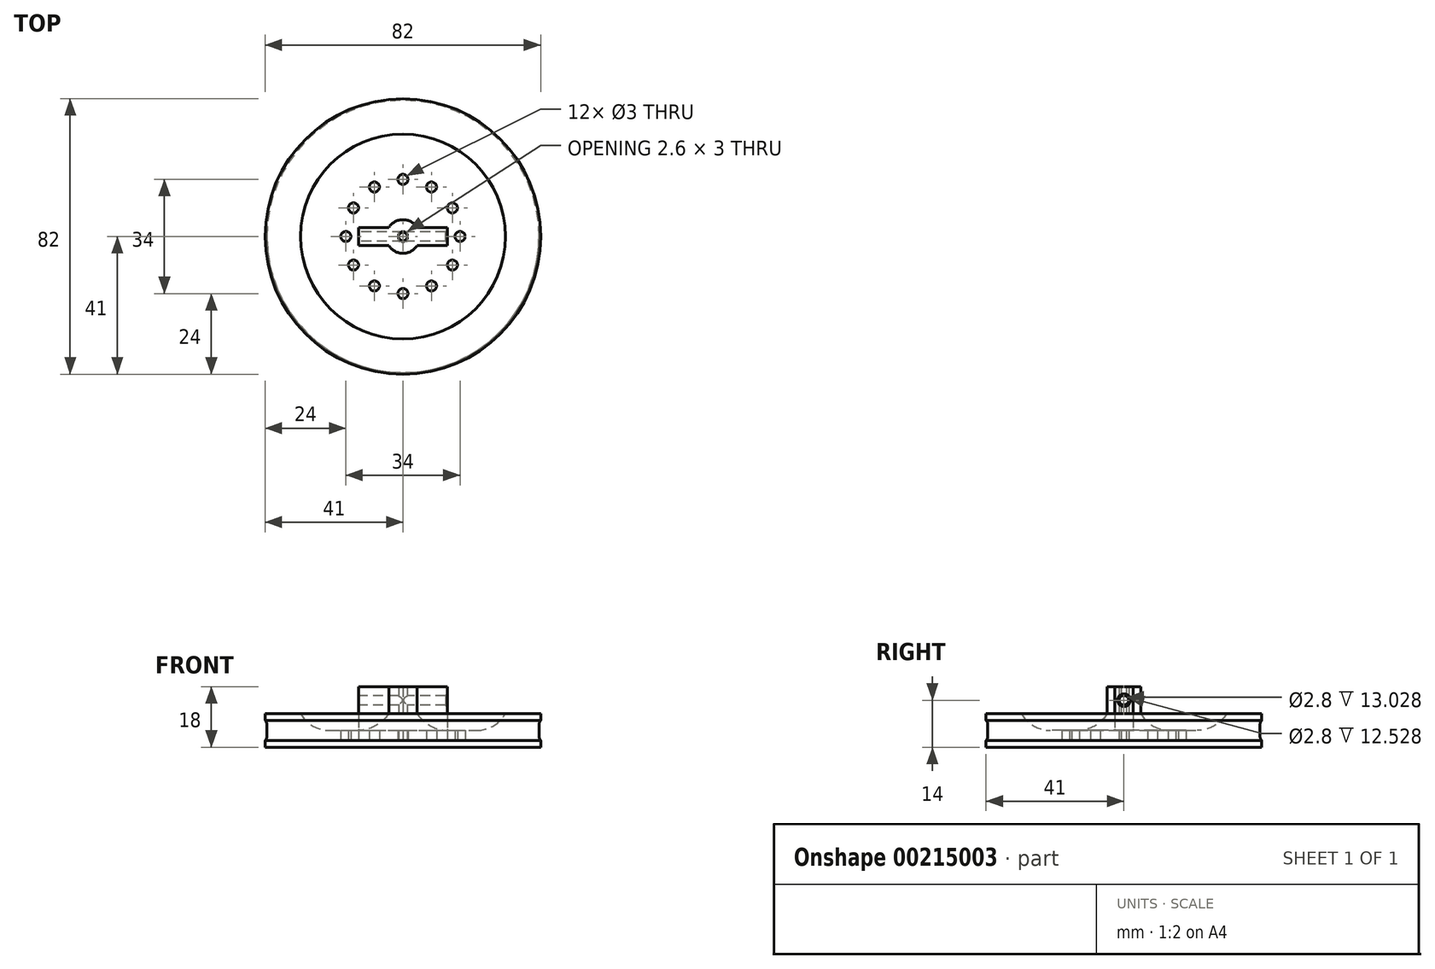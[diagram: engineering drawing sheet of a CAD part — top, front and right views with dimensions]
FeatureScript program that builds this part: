
annotation { "Feature Type Name" : "Feature", "Feature Type Description" : "" }
export const myFeature = defineFeature(function(context is Context, id is Id, definition is map)
    precondition{}
    {
        {
            var Q0;
            Q0=qCreatedBy(makeId("Front.planeOp"),FACE);
            var sketch = newSketch(context, id + "F0", { "sketchPlane" : qUnion([Q0])});
            skLineSegment(sketch, "E0", {"start": v(0, 0) * mm, "end": v(41, 0) * mm});
            skLineSegment(sketch, "E1", {"start": v(41, 10) * mm, "end": v(30.5, 10) * mm});
            skLineSegment(sketch, "E2", {"start": v(30.5, 10) * mm, "end": v(30.5, 5) * mm});
            skLineSegment(sketch, "E3", {"start": v(30.5, 5) * mm, "end": v(5, 5) * mm});
            skLineSegment(sketch, "E4", {"start": v(5, 5) * mm, "end": v(5, 10) * mm});
            skLineSegment(sketch, "E5", {"start": v(5, 10) * mm, "end": v(0, 10) * mm});
            skLineSegment(sketch, "E6", {"start": v(0, 10) * mm, "end": v(0, 0) * mm});
            skLineSegment(sketch, "E7", {"start": v(41, 0) * mm, "end": v(41, 2) * mm});
            skLineSegment(sketch, "E8", {"start": v(41, 2) * mm, "end": v(40.5, 2) * mm});
            skLineSegment(sketch, "E9", {"start": v(40.5, 2) * mm, "end": v(40.5, 8) * mm});
            skLineSegment(sketch, "E10", {"start": v(40.5, 8) * mm, "end": v(41, 8) * mm});
            skLineSegment(sketch, "E11", {"start": v(41, 8) * mm, "end": v(41, 10) * mm});
            skSolve(sketch);
        }
        {
            var Q0;
            Q0 = qSketchRegion(id + "F0", true);
            var Q1;
            Q1=sQuery(id+"F0.wireOp",EDGE,"E6");
            revolve(context, id + "F1", {"entities" : qUnion([Q0]), "axis" : qUnion([Q1]), "revolveType" : RevolveType.FULL});
        }
        {
            var Q0;
            Q0=makeQuery(id+"F1.opRevolve","SWEPT_EDGE",EDGE,{"disambiguationData":[OSD([sQuery(id+"F0.wireOp",EDGE,"E3"),sQuery(id+"F0.wireOp",EDGE,"E4")])]});
            fillet(context, id + "F2", {"entities" : qUnion([Q0]), "radius" : 10 * mm, "tangentPropagation" : true, "allowEdgeOverflow" : false});
        }
        {
            var Q0;
            Q0=makeQuery(id+"F1.opRevolve","SWEPT_EDGE",EDGE,{"disambiguationData":[OSD([sQuery(id+"F0.wireOp",EDGE,"E2"),sQuery(id+"F0.wireOp",EDGE,"E3")])]});
            fillet(context, id + "F3", {"entities" : qUnion([Q0]), "radius" : 10 * mm, "tangentPropagation" : true, "allowEdgeOverflow" : false});
        }
        {
            var Q0;
            Q0=makeQuery(id+"F1.opRevolve","SWEPT_FACE",FACE,{"disambiguationData":[OSD([sQuery(id+"F0.wireOp",EDGE,"E5")])]});
            var sketch = newSketch(context, id + "F4", { "sketchPlane" : qUnion([Q0])});
            skCircle(sketch, "E12.cCircle", {"center": v(0, 0) * mm, "radius": 1.5 * mm, "construction": true});
            skLineSegment(sketch, "E12.0", {"start": v(0, -1.5) * mm, "end": v(-1.3, -0.75) * mm});
            skLineSegment(sketch, "E12.1", {"start": v(-1.3, -0.75) * mm, "end": v(-1.3, 0.75) * mm});
            skLineSegment(sketch, "E12.2", {"start": v(-1.3, 0.75) * mm, "end": v(0, 1.5) * mm});
            skLineSegment(sketch, "E12.3", {"start": v(0, 1.5) * mm, "end": v(1.3, 0.75) * mm});
            skLineSegment(sketch, "E12.4", {"start": v(1.3, 0.75) * mm, "end": v(1.3, -0.75) * mm});
            skLineSegment(sketch, "E12.5", {"start": v(1.3, -0.75) * mm, "end": v(0, -1.5) * mm});
            skArc(sketch, "E13", {"start": v(-4.2, -2.71) * mm, "mid": v(5, 0) * mm, "end": v(-4.2, 2.71) * mm});
            skLineSegment(sketch, "E14", {"start": v(-4.2, -2.71) * mm, "end": v(-4.2, 2.71) * mm});
            skSolve(sketch);
        }
        {
            var Q0;
            Q0 = qSketchRegion(id + "F4", true);
            extrude(context, id + "F5", {"entities" : qUnion([Q0]), "operationType" : NewBodyOperationType.ADD, "depth" : 8 * mm});
        }
        {
            var Q0;
            Q0=makeQuery(id+"F5.opExtrude","SWEPT_FACE",FACE,{"disambiguationData":[OSD([sQuery(id+"F4.wireOp",EDGE,"E14")])]});
            extrude(context, id + "F6", {"entities" : qUnion([Q0]), "operationType" : NewBodyOperationType.ADD, "depth" : 9 * mm});
        }
        {
            var Q0;
            Q0=makeQuery(id+"F6.opExtrude","CAP_FACE",FACE,{"disambiguationData":[OSD([sQuery(id+"F4.wireOp",EDGE,"E14")])],"isStart":false});
            var sketch = newSketch(context, id + "F7", { "sketchPlane" : qUnion([Q0])});
            skCircle(sketch, "E15", {"center": v(0, 14) * mm, "radius": 1.4 * mm});
            skPoint(sketch, "E15.centerSnap0", {"position": v(0, 18) * mm});
            skSolve(sketch);
        }
        {
            var Q0;
            Q0 = qSketchRegion(id + "F7", true);
            extrude(context, id + "F8", {"entities" : qUnion([Q0]), "operationType" : NewBodyOperationType.REMOVE, "endBound" : BoundingType.THROUGH_ALL, "oppositeDirection" : true, "depth" : 25 * mm});
        }
        {
            var Q0;
            {var subQ0=sQuery(id+"F4.wireOp",EDGE,"E14");Q0=makeQuery(id+"F6.boolean.opBoolean","MERGE",FACE,{"derivedFrom":[makeQuery(id+"F5.opExtrude","CAP_FACE",FACE,{"disambiguationData":[OSD([sQuery(id+"F4.wireOp",EDGE,"E12.0"),sQuery(id+"F4.wireOp",EDGE,"E12.1"),sQuery(id+"F4.wireOp",EDGE,"E12.2"),sQuery(id+"F4.wireOp",EDGE,"E12.3"),sQuery(id+"F4.wireOp",EDGE,"E12.4"),sQuery(id+"F4.wireOp",EDGE,"E12.5"),sQuery(id+"F4.wireOp",EDGE,"E13"),subQ0])],"isStart":false}),makeQuery(id+"F6.opExtrude","SWEPT_FACE",FACE,{"disambiguationData":[OSD([subQ0]),TDD([makeQuery(id+"F5.opExtrude","CAP_EDGE",EDGE,{"disambiguationData":[OSD([subQ0])],"isStart":false})])]})]});}
            var sketch = newSketch(context, id + "F9", { "sketchPlane" : qUnion([Q0])});
            skLineSegment(sketch, "E16.0", {"start": v(1.3, -0.75) * mm, "end": v(0, -1.5) * mm});
            skLineSegment(sketch, "E16.1", {"start": v(0, -1.5) * mm, "end": v(-1.3, -0.75) * mm});
            skLineSegment(sketch, "E16.2", {"start": v(-1.3, -0.75) * mm, "end": v(-1.3, 0.75) * mm});
            skLineSegment(sketch, "E16.3", {"start": v(-1.3, 0.75) * mm, "end": v(0, 1.5) * mm});
            skLineSegment(sketch, "E16.4", {"start": v(0, 1.5) * mm, "end": v(1.3, 0.75) * mm});
            skLineSegment(sketch, "E16.5", {"start": v(1.3, 0.75) * mm, "end": v(1.3, -0.75) * mm});
            skSolve(sketch);
        }
        {
            var Q0;
            Q0 = qSketchRegion(id + "F9", true);
            extrude(context, id + "F10", {"entities" : qUnion([Q0]), "operationType" : NewBodyOperationType.REMOVE, "endBound" : BoundingType.THROUGH_ALL, "oppositeDirection" : true, "depth" : 25 * mm});
        }
        {
            var Q0;
            Q0=makeQuery(id+"F1.opRevolve","SWEPT_EDGE",EDGE,{"disambiguationData":[OSD([sQuery(id+"F0.wireOp",EDGE,"E8"),sQuery(id+"F0.wireOp",EDGE,"E9")])]});
            var Q1;
            Q1=makeQuery(id+"F1.opRevolve","SWEPT_EDGE",EDGE,{"disambiguationData":[OSD([sQuery(id+"F0.wireOp",EDGE,"E9"),sQuery(id+"F0.wireOp",EDGE,"E10")])]});
            fillet(context, id + "F11", {"entities" : qUnion([Q0, Q1]), "radius" : 2 * mm, "tangentPropagation" : true, "allowEdgeOverflow" : false});
        }
        {
            var Q0;
            Q0=makeQuery(id+"F6.opExtrude","CAP_FACE",FACE,{"disambiguationData":[OSD([sQuery(id+"F4.wireOp",EDGE,"E14")])],"isStart":false});
            extrude(context, id + "F12", {"entities" : qUnion([Q0]), "operationType" : NewBodyOperationType.ADD, "oppositeDirection" : true, "depth" : 26.4 * mm});
        }
        {
            var Q0;
            Q0=makeQuery(id+"F1.opRevolve","SWEPT_FACE",FACE,{"disambiguationData":[OSD([sQuery(id+"F0.wireOp",EDGE,"E0")])]});
            var sketch = newSketch(context, id + "F13", { "sketchPlane" : qUnion([Q0])});
            skLineSegment(sketch, "E17.0", {"start": v(1.3, -0.75) * mm, "end": v(1.3, 0.75) * mm});
            skLineSegment(sketch, "E17.1", {"start": v(0, -1.5) * mm, "end": v(1.3, -0.75) * mm});
            skLineSegment(sketch, "E17.2", {"start": v(-1.3, -0.75) * mm, "end": v(0, -1.5) * mm});
            skLineSegment(sketch, "E17.3", {"start": v(-1.3, 0.75) * mm, "end": v(-1.3, -0.75) * mm});
            skLineSegment(sketch, "E17.4", {"start": v(0, 1.5) * mm, "end": v(-1.3, 0.75) * mm});
            skLineSegment(sketch, "E17.5", {"start": v(1.3, 0.75) * mm, "end": v(0, 1.5) * mm});
            skSolve(sketch);
        }
        {
            var Q0;
            Q0 = qSketchRegion(id + "F13", true);
            extrude(context, id + "F14", {"entities" : qUnion([Q0]), "operationType" : NewBodyOperationType.REMOVE, "endBound" : BoundingType.THROUGH_ALL, "oppositeDirection" : true, "depth" : 25 * mm});
        }
        {
            var Q0;
            Q0=makeQuery(id+"F1.opRevolve","SWEPT_FACE",FACE,{"disambiguationData":[OSD([sQuery(id+"F0.wireOp",EDGE,"E1")])]});
            var sketch = newSketch(context, id + "F15", { "sketchPlane" : qUnion([Q0])});
            skLineSegment(sketch, "E18.0", {"start": v(13.2, 2.71) * mm, "end": v(4.2, 2.71) * mm});
            skLineSegment(sketch, "E18.1", {"start": v(13.2, -2.71) * mm, "end": v(13.2, 2.71) * mm});
            skArc(sketch, "E18.2", {"start": v(4.2, 2.71) * mm, "mid": v(0, 5) * mm, "end": v(-4.2, 2.71) * mm});
            skLineSegment(sketch, "E18.3", {"start": v(-13.2, 2.71) * mm, "end": v(-4.2, 2.71) * mm});
            skLineSegment(sketch, "E18.4", {"start": v(-13.2, -2.71) * mm, "end": v(-13.2, 2.71) * mm});
            skLineSegment(sketch, "E18.5", {"start": v(-13.2, -2.71) * mm, "end": v(-4.2, -2.71) * mm});
            skArc(sketch, "E18.6", {"start": v(-4.2, -2.71) * mm, "mid": v(0, -5) * mm, "end": v(4.2, -2.71) * mm});
            skLineSegment(sketch, "E18.7", {"start": v(13.2, -2.71) * mm, "end": v(4.2, -2.71) * mm});
            skSolve(sketch);
        }
        {
            var Q0;
            Q0 = qSketchRegion(id + "F15", true);
            var Q1;
            Q1=makeQuery(id+"F1.opRevolve","SWEPT_FACE",FACE,{"disambiguationData":[OSD([sQuery(id+"F0.wireOp",EDGE,"E3")])]});
            extrude(context, id + "F16", {"entities" : qUnion([Q0]), "operationType" : NewBodyOperationType.ADD, "endBound" : BoundingType.UP_TO_SURFACE, "oppositeDirection" : true, "endBoundEntityFace" : qUnion([Q1]), "depth" : 25 * mm});
        }
        {
            var Q0;
            Q0=makeQuery(id+"F8.boolean.opBoolean","COPY",EDGE,{"derivedFrom":makeQuery(id+"F8.opExtrude","CAP_EDGE",EDGE,{"disambiguationData":[OSD([sQuery(id+"F7.wireOp",EDGE,"E15")])],"isStart":true})});
            var Q1;
            Q1=makeQuery(id+"F12.opExtrude","CAP_EDGE",EDGE,{"disambiguationData":[OSD([sQuery(id+"F7.wireOp",EDGE,"E15")])],"isStart":false});
            chamfer(context, id + "F17", {"entities" : qUnion([Q0, Q1]), "width" : 0.5 * mm, "tangentPropagation" : true});
        }
        {
            var Q0;
            Q0=makeQuery(id+"F1.opRevolve","SWEPT_FACE",FACE,{"disambiguationData":[OSD([sQuery(id+"F0.wireOp",EDGE,"E0")])]});
            var sketch = newSketch(context, id + "F18", { "sketchPlane" : qUnion([Q0])});
            skCircle(sketch, "E19", {"center": v(0, 17) * mm, "radius": 1.5 * mm});
            skCircle(sketch, "E20.1.0", {"center": v(-8.5, 14.72) * mm, "radius": 1.5 * mm});
            skCircle(sketch, "E20.2.0", {"center": v(-14.72, 8.5) * mm, "radius": 1.5 * mm});
            skCircle(sketch, "E20.3.0", {"center": v(-17, 0) * mm, "radius": 1.5 * mm});
            skCircle(sketch, "E20.4.0", {"center": v(-14.72, -8.5) * mm, "radius": 1.5 * mm});
            skCircle(sketch, "E20.5.0", {"center": v(-8.5, -14.72) * mm, "radius": 1.5 * mm});
            skCircle(sketch, "E20.6.0", {"center": v(0, -17) * mm, "radius": 1.5 * mm});
            skCircle(sketch, "E20.7.0", {"center": v(8.5, -14.72) * mm, "radius": 1.5 * mm});
            skCircle(sketch, "E20.8.0", {"center": v(14.72, -8.5) * mm, "radius": 1.5 * mm});
            skCircle(sketch, "E20.9.0", {"center": v(17, 0) * mm, "radius": 1.5 * mm});
            skCircle(sketch, "E20.10.0", {"center": v(14.72, 8.5) * mm, "radius": 1.5 * mm});
            skCircle(sketch, "E20.11.0", {"center": v(8.5, 14.72) * mm, "radius": 1.5 * mm});
            skPoint(sketch, "E20.center", {"position": v(0, 0) * mm});
            skSolve(sketch);
        }
        {
            var Q0;
            Q0 = qSketchRegion(id + "F18", true);
            extrude(context, id + "F19", {"entities" : qUnion([Q0]), "operationType" : NewBodyOperationType.REMOVE, "endBound" : BoundingType.THROUGH_ALL, "oppositeDirection" : true, "depth" : 25 * mm});
        }
    });
